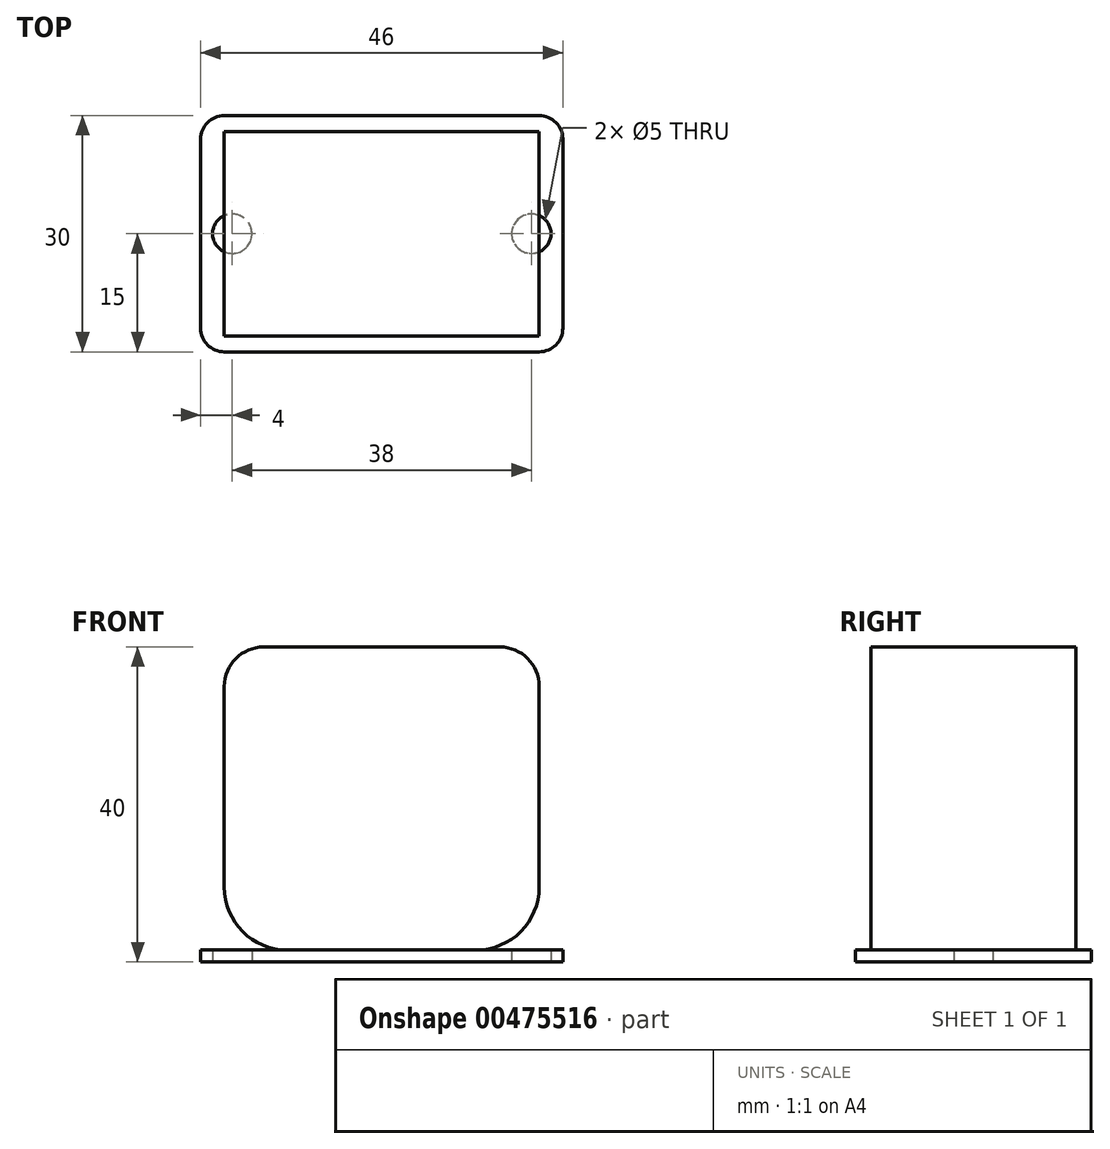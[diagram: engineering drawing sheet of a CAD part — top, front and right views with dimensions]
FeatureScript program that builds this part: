
annotation { "Feature Type Name" : "Feature", "Feature Type Description" : "" }
export const myFeature = defineFeature(function(context is Context, id is Id, definition is map)
    precondition{}
    {
        {
            var Q0;
            Q0=qCreatedBy(makeId("Top.planeOp"),FACE);
            var sketch = newSketch(context, id + "F0", { "sketchPlane" : qUnion([Q0])});
            skLineSegment(sketch, "E0.bottom", {"start": v(20, -15) * mm, "end": v(-20, -15) * mm});
            skLineSegment(sketch, "E0.top", {"start": v(20, 15) * mm, "end": v(-20, 15) * mm});
            skLineSegment(sketch, "E0.left", {"start": v(23, -12) * mm, "end": v(23, 12) * mm});
            skLineSegment(sketch, "E0.right", {"start": v(-23, -12) * mm, "end": v(-23, 12) * mm});
            skPoint(sketch, "E0.middle", {"position": v(0, 0) * mm});
            skPoint(sketch, "E1.visualSharp", {"position": v(-23, 15) * mm});
            skArc(sketch, "E1.filletArc", {"start": v(-20, 15) * mm, "mid": v(-22.12, 14.12) * mm, "end": v(-23, 12) * mm});
            skPoint(sketch, "E2.visualSharp", {"position": v(23, 15) * mm});
            skArc(sketch, "E2.filletArc", {"start": v(23, 12) * mm, "mid": v(22.12, 14.12) * mm, "end": v(20, 15) * mm});
            skPoint(sketch, "E3.visualSharp", {"position": v(23, -15) * mm});
            skArc(sketch, "E3.filletArc", {"start": v(20, -15) * mm, "mid": v(22.12, -14.12) * mm, "end": v(23, -12) * mm});
            skPoint(sketch, "E4.visualSharp", {"position": v(-23, -15) * mm});
            skArc(sketch, "E4.filletArc", {"start": v(-23, -12) * mm, "mid": v(-22.12, -14.12) * mm, "end": v(-20, -15) * mm});
            skCircle(sketch, "E5", {"center": v(-19, 0) * mm, "radius": 2.5 * mm});
            skCircle(sketch, "E6.MirrorC", {"center": v(19, 0) * mm, "radius": 2.5 * mm});
            skSolve(sketch);
        }
        {
            var Q0;
            Q0=makeQuery(id+"F0.imprint","IMPRINT",FACE,{"disambiguationData":[TD([[makeQuery(id+"F0.imprint","IMPRINT",EDGE,{"derivedFrom":sQuery(id+"F0.wireOp",EDGE,"E0.bottom")}),-1.0]])]});
            extrude(context, id + "F1", {"entities" : qUnion([Q0]), "depth" : 1.5 * mm});
        }
        {
            var Q0;
            Q0=makeQuery(id+"F1.opExtrude","CAP_FACE",FACE,{"disambiguationData":[OSD([sQuery(id+"F0.wireOp",EDGE,"E0.bottom"),sQuery(id+"F0.wireOp",EDGE,"E0.top"),sQuery(id+"F0.wireOp",EDGE,"E0.left"),sQuery(id+"F0.wireOp",EDGE,"E0.right"),sQuery(id+"F0.wireOp",EDGE,"E1.filletArc"),sQuery(id+"F0.wireOp",EDGE,"E2.filletArc"),sQuery(id+"F0.wireOp",EDGE,"E3.filletArc"),sQuery(id+"F0.wireOp",EDGE,"E4.filletArc"),sQuery(id+"F0.wireOp",EDGE,"E5"),sQuery(id+"F0.wireOp",EDGE,"E6.MirrorC")])],"isStart":false});
            var sketch = newSketch(context, id + "F2", { "sketchPlane" : qUnion([Q0])});
            skLineSegment(sketch, "E7.bottom", {"start": v(20, -13) * mm, "end": v(-20, -13) * mm});
            skLineSegment(sketch, "E7.top", {"start": v(20, 13) * mm, "end": v(-20, 13) * mm});
            skLineSegment(sketch, "E7.left", {"start": v(20, -13) * mm, "end": v(20, 13) * mm});
            skLineSegment(sketch, "E7.right", {"start": v(-20, -13) * mm, "end": v(-20, 13) * mm});
            skPoint(sketch, "E7.middle", {"position": v(0, 0) * mm});
            skSolve(sketch);
        }
        {
            var Q0;
            Q0=makeQuery(id+"F2.imprint","IMPRINT",FACE,{"disambiguationData":[TD([[makeQuery(id+"F2.imprint","IMPRINT",EDGE,{"derivedFrom":sQuery(id+"F2.wireOp",EDGE,"E7.bottom")}),-1.0]])]});
            var Q1;
            {var subQ0=sQuery(id+"F2.wireOp",EDGE,"E7.right");var subQ1=makeQuery(id+"F1.opExtrude","CAP_EDGE",EDGE,{"disambiguationData":[OSD([sQuery(id+"F0.wireOp",EDGE,"E5")])],"isStart":false});var subQ2=makeQuery(id+"F2.imprint","INTERSECT",VERTEX,{"disambiguationData":[OD(0.0)],"derivedFrom":[subQ1,subQ0]});Q1=makeQuery(id+"F2.imprint","IMPRINT",FACE,{"disambiguationData":[TD([[makeQuery(id+"F2.imprint","IMPRINT",EDGE,{"disambiguationData":[TD([[subQ2,-1.0]])],"derivedFrom":subQ0}),-1.0]])]});}
            var Q2;
            {var subQ0=sQuery(id+"F2.wireOp",EDGE,"E7.left");var subQ1=makeQuery(id+"F1.opExtrude","CAP_EDGE",EDGE,{"disambiguationData":[OSD([sQuery(id+"F0.wireOp",EDGE,"E6.MirrorC")])],"isStart":false});var subQ2=makeQuery(id+"F2.imprint","INTERSECT",VERTEX,{"disambiguationData":[OD(0.0)],"derivedFrom":[subQ1,subQ0]});Q2=makeQuery(id+"F2.imprint","IMPRINT",FACE,{"disambiguationData":[TD([[makeQuery(id+"F2.imprint","IMPRINT",EDGE,{"disambiguationData":[TD([[subQ2,-1.0]])],"derivedFrom":subQ0}),1.0]])]});}
            extrude(context, id + "F3", {"entities" : qUnion([Q0, Q1, Q2]), "depth" : 38.5 * mm});
        }
        {
            var Q0;
            Q0=makeQuery(id+"F3.opExtrude","CAP_EDGE",EDGE,{"disambiguationData":[OSD([sQuery(id+"F2.wireOp",EDGE,"E7.right")])],"isStart":true});
            var Q1;
            Q1=makeQuery(id+"F3.opExtrude","CAP_EDGE",EDGE,{"disambiguationData":[OSD([sQuery(id+"F2.wireOp",EDGE,"E7.left")])],"isStart":true});
            fillet(context, id + "F4", {"entities" : qUnion([Q0, Q1]), "radius" : 8 * mm, "tangentPropagation" : true, "allowEdgeOverflow" : false});
        }
        {
            var Q0;
            Q0=makeQuery(id+"F3.opExtrude","CAP_EDGE",EDGE,{"disambiguationData":[OSD([sQuery(id+"F2.wireOp",EDGE,"E7.right")])],"isStart":false});
            var Q1;
            Q1=makeQuery(id+"F3.opExtrude","CAP_EDGE",EDGE,{"disambiguationData":[OSD([sQuery(id+"F2.wireOp",EDGE,"E7.left")])],"isStart":false});
            fillet(context, id + "F5", {"entities" : qUnion([Q0, Q1]), "radius" : 5 * mm, "tangentPropagation" : true, "allowEdgeOverflow" : false});
        }
    });
